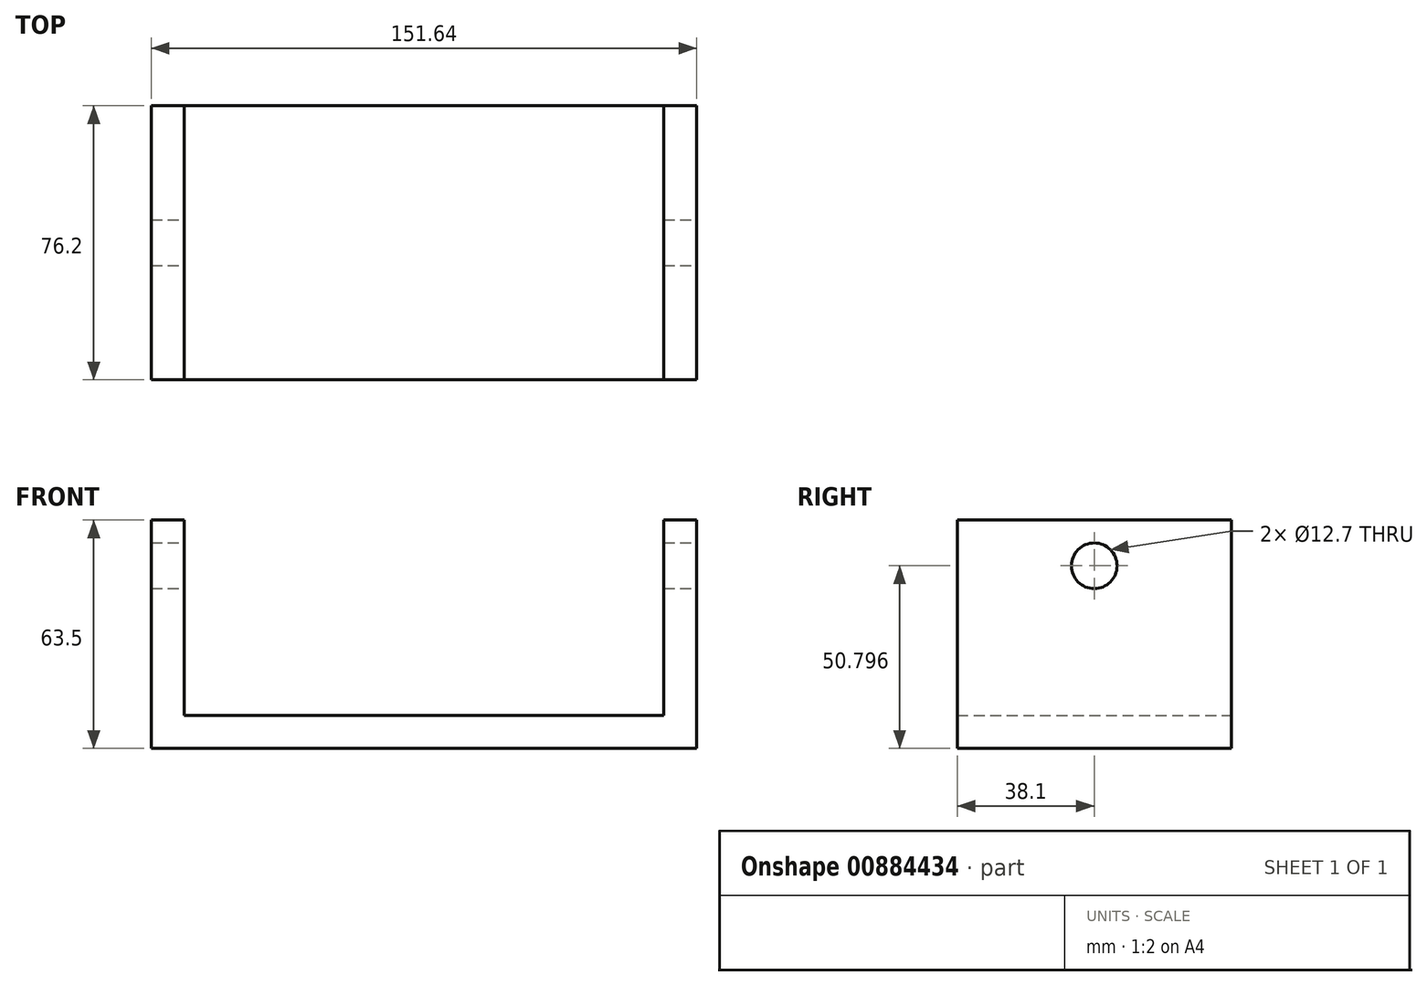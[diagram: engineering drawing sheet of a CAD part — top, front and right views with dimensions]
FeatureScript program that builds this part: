
annotation { "Feature Type Name" : "Feature", "Feature Type Description" : "" }
export const myFeature = defineFeature(function(context is Context, id is Id, definition is map)
    precondition{}
    {
        {
            var Q0;
            Q0=qCreatedBy(makeId("Front.planeOp"),FACE);
            var sketch = newSketch(context, id + "F0", { "sketchPlane" : qUnion([Q0])});
            skLineSegment(sketch, "E0.top", {"start": v(-38.67, 0) * mm, "end": v(94.68, 0) * mm});
            skLineSegment(sketch, "E0.left", {"start": v(-38.67, 54.36) * mm, "end": v(-38.67, 0) * mm});
            skLineSegment(sketch, "E0.right", {"start": v(94.68, 54.36) * mm, "end": v(94.68, 0) * mm});
            skLineSegment(sketch, "E1", {"start": v(-38.67, 54.36) * mm, "end": v(-47.82, 54.36) * mm});
            skLineSegment(sketch, "E2", {"start": v(-47.82, 54.36) * mm, "end": v(-47.82, -9.14) * mm});
            skLineSegment(sketch, "E3", {"start": v(-47.82, -9.14) * mm, "end": v(103.82, -9.14) * mm});
            skLineSegment(sketch, "E4", {"start": v(103.82, -9.14) * mm, "end": v(103.82, 54.36) * mm});
            skLineSegment(sketch, "E5", {"start": v(94.68, 54.36) * mm, "end": v(103.82, 54.36) * mm});
            skSolve(sketch);
        }
        {
            var Q0;
            Q0=makeQuery(id+"F0.imprint","IMPRINT",FACE,{"disambiguationData":[TD([[makeQuery(id+"F0.imprint","IMPRINT",EDGE,{"derivedFrom":sQuery(id+"F0.wireOp",EDGE,"E0.top")}),-1.0]])]});
            extrude(context, id + "F1", {"entities" : qUnion([Q0]), "depth" : 76.2 * mm, "offsetDistance" : 25.4 * mm});
        }
        {
            var Q0;
            Q0=makeQuery(id+"F1.opExtrude","SWEPT_FACE",FACE,{"disambiguationData":[OSD([sQuery(id+"F0.wireOp",EDGE,"E4")])]});
            var sketch = newSketch(context, id + "F2", { "sketchPlane" : qUnion([Q0])});
            skCircle(sketch, "E6", {"center": v(-38.1, 41.66) * mm, "radius": 6.35 * mm});
            skSolve(sketch);
        }
        {
            var Q0;
            Q0=makeQuery(id+"F2.imprint","IMPRINT",FACE,{"disambiguationData":[TD([[makeQuery(id+"F2.imprint","IMPRINT",EDGE,{"derivedFrom":sQuery(id+"F2.wireOp",EDGE,"E6")}),1.0]])]});
            extrude(context, id + "F3", {"entities" : qUnion([Q0]), "operationType" : NewBodyOperationType.REMOVE, "endBound" : BoundingType.THROUGH_ALL, "oppositeDirection" : true, "depth" : 25.4 * mm, "offsetDistance" : 25.4 * mm});
        }
    });
